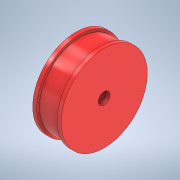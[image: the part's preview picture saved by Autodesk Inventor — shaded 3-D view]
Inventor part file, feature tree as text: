
AUTODESK INVENTOR PART (.ipt)
format: ipt  version: 2020 (Build 240168000, 168)  size: 143,360 bytes
history: native  units: in
note: dims shown in document units (in); Inventor stores cm internally (conversion verified against a paired STEP export)
features: extrude x3, sketch x3
ambient origin geometry x8: Origin, YZ Plane, XZ Plane, XY Plane, X Axis, Y Axis, Z Axis, Center Point
bodies: Solid1 (feature_tree)
feature tree (6):
  extrude  "Extrusion1"  Depth=0.5in
  extrude  "Extrusion2"  Depth=1.0in
  extrude  "Extrusion3"  Depth=0.2in TaperAngle=0.0deg
  sketch  "Sketch1"  dims[d0=0.5in d1=4.0in]
  sketch  "Sketch2"  dims[d2=1.0in d3=0.0in d4=4.25in]
  sketch  "Sketch3"  dims[d5=0.2in d6=0.0in d7=0.2in d8=0.0in]
